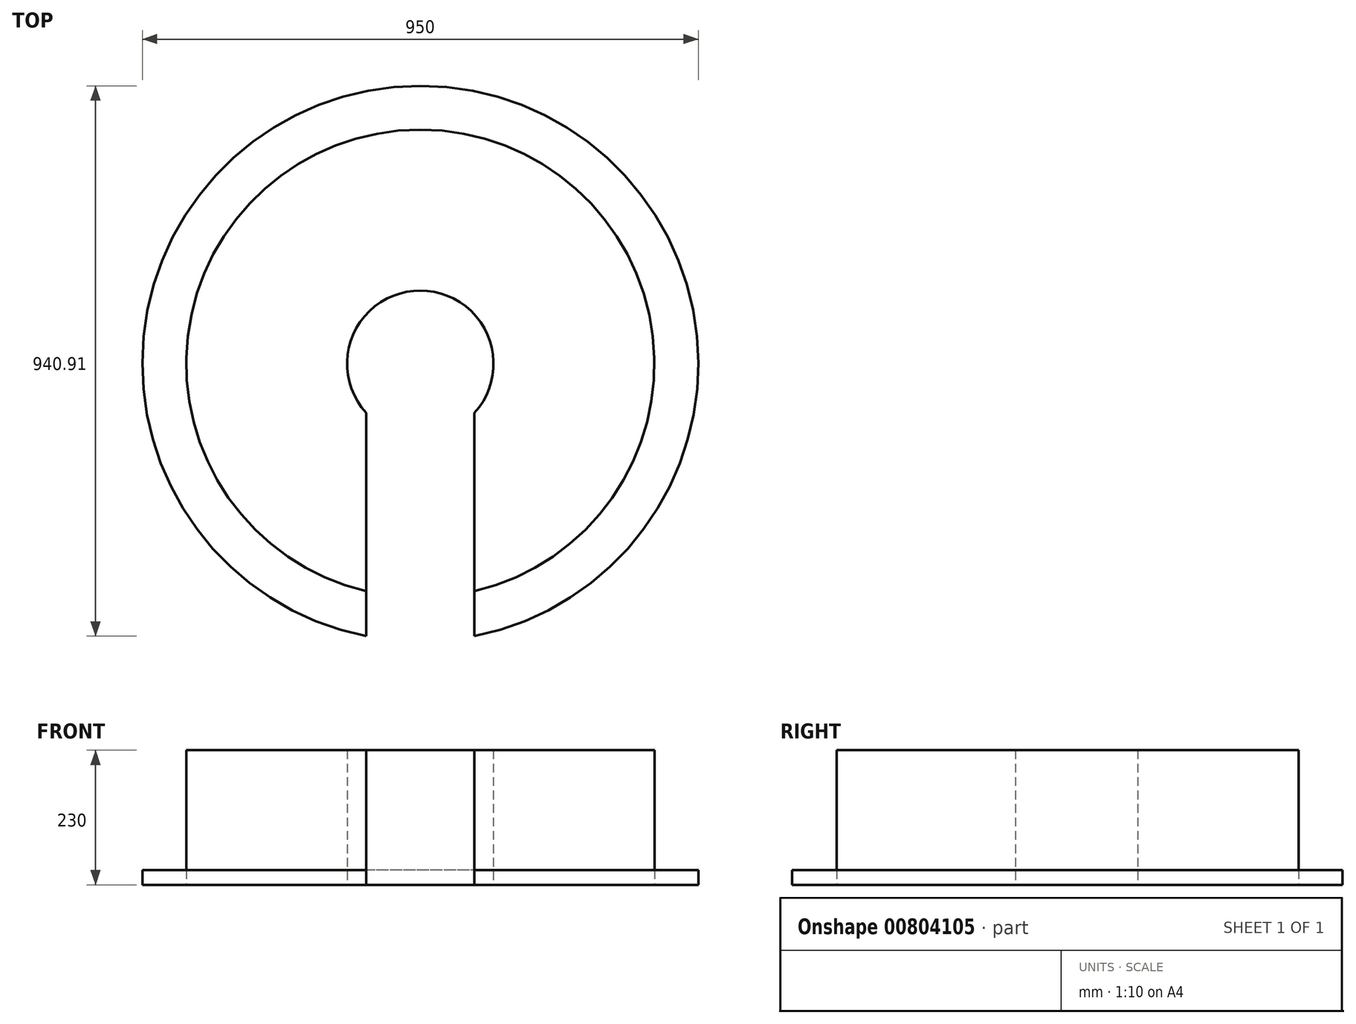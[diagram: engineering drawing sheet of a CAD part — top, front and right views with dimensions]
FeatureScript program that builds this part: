
annotation { "Feature Type Name" : "Feature", "Feature Type Description" : "" }
export const myFeature = defineFeature(function(context is Context, id is Id, definition is map)
    precondition{}
    {
        {
            var Q0;
            Q0=qCreatedBy(makeId("Top.planeOp"),FACE);
            var sketch = newSketch(context, id + "F0", { "sketchPlane" : qUnion([Q0]), "asVersion" : FeatureScriptVersionNumber.V422_RIB_DELETE_ERROR_BODIES});
            skArc(sketch, "E0", {"start": v(92.5, -389.16) * mm, "mid": v(0, 400) * mm, "end": v(-92.5, -389.16) * mm});
            skArc(sketch, "E1", {"start": v(92.5, -84.08) * mm, "mid": v(0, 125) * mm, "end": v(-92.5, -84.08) * mm});
            skLineSegment(sketch, "E2", {"start": v(-92.5, -84.08) * mm, "end": v(-92.5, -465.9) * mm});
            skLineSegment(sketch, "E3", {"start": v(0, 0) * mm, "end": v(0, -80.35) * mm, "construction": true});
            skLineSegment(sketch, "E4.MirrorCS", {"start": v(92.5, -84.08) * mm, "end": v(92.5, -465.9) * mm});
            skPoint(sketch, "E5.orphan", {"position": v(-92.5, -12.09) * mm});
            skPoint(sketch, "E6.orphan", {"position": v(92.5, -12.09) * mm});
            skPoint(sketch, "E7.orphan", {"position": v(-92.5, -439.56) * mm});
            skPoint(sketch, "E8.orphan", {"position": v(92.5, -439.56) * mm});
            skCircle(sketch, "E9", {"center": v(0, 0) * mm, "radius": 475 * mm});
            skSolve(sketch);
        }
        {
            var Q0;
            {var subQ0=sQuery(id+"F0.wireOp",EDGE,"E0");Q0=makeQuery(id+"F0.imprint","IMPRINT",FACE,{"disambiguationData":[TD([[makeQuery(id+"F0.imprint","IMPRINT",EDGE,{"derivedFrom":subQ0}),1.0]])]});}
            extrude(context, id + "F1", {"entities" : qUnion([Q0]), "depth" : 230 * mm});
        }
        {
            var Q0;
            {var subQ0=sQuery(id+"F0.wireOp",EDGE,"E0");Q0=makeQuery(id+"F0.imprint","IMPRINT",FACE,{"disambiguationData":[TD([[makeQuery(id+"F0.imprint","IMPRINT",EDGE,{"derivedFrom":subQ0}),-1.0]])]});}
            extrude(context, id + "F2", {"entities" : qUnion([Q0]), "depth" : 25 * mm});
        }
    });
